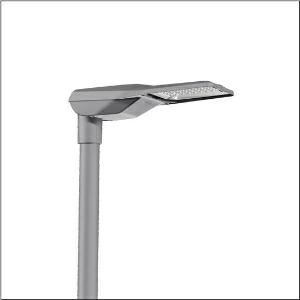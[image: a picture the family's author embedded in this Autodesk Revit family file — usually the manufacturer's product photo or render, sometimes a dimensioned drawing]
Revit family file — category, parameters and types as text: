
# Revit family: streetlight_sl_21_iq_mini___p1_0a_5xe2a31d08gb_969e
name_source: partatom
category: Lighting Fixtures
units: mm (PartAtom-declared; Revit-internal decimal feet)

## family parameters
Cut with Voids When Loaded = No
Host = Face
Light Source = No
Part Type = Normal
Room Calculation Point = No
Round Connector Dimension = Use Diameter
Shared = No

## types (1)
- --- (1 x LED, 5680 lm, 37.1 W, 3000K)
    Apparent Load = 37 VA
    CIE Flux Codes = 21 50 90 100 100
    Color Rendering = 70
    Color Temperature = 3000K
    Default Elevation = 1800 mm
    Description = Streetlight SL 21 iQ mini, mast luminaire, primary light control with lens, of PMMA, primary optical cover: cover, of toughened safety glass, transparent, light distribution: P1.0a, light emission: direct distribution, primary light characteristic: asymmetric, installation type: post-top, side-entry, LED, High Power LED, rated luminous flux: 5.680lm, luminous efficacy: 153lm/W, light colour: 730, colour temperature: 3000K, control: Auto-Match, Temp-Guard, Lumen-Switch, Night-Set, Smart-Wire, Light-Fading, Desk-Remote (wireless, voltage-free reading and setting of iQ features in the workshop via application-optimized NFC function/RFID function), optimised constant luminous flux control (CLO 2.0), presetting dimming linear, mains connection: 220..240V, AC, 50/60Hz, start of lifetime: 37W, end of service life: 39W, reduction: 18W, luminaire housing, of diecast aluminium, powder-coated, Siteco® metallic grey (DB 702S), corrosivity category C5 mid according to DIN EN ISO 12944, please order mast flange separately, inclination adjustable: 0°, 5°, 10°, 15°, sealing non-destructively replaceable, multi-level sealing system, length: 628mm, width: 235mm, height: 110mm, mast flange for spigot size: 42mm (side-entry): 5XC10008XM4, 60/48mm (side-entry/post-top): 5XC10108XM2, 76/60mm (side-entry/post-top): 5XC10108XM1, protection rating (complete): IP66, insulation class (complete): insulation class II (safety insulation), certification: CE, ENEC, ENEC+, VDE, impact resistance: IK09, permissible operating ambient temperature for outdoor applications: -40..+50°C, standard-compliant lighting for roads and squares, packaging unit: 1 piece

Light Distribution: P1.0a
    Height = 110 mm
    Lamp = 1 x LED
    Lamp Light Flux = 5680 lm
    Lamp Power = 37.1 W
    Lamp count = 1
    Length = 625 mm
    Luminous efficacy = 153 lm/W
    Manufacturer = Siteco
    ModVariant = No
    Model = 5XE2A31D08GB
    Number of Poles = 1
    OnlyDefault = Yes
    Power Factor = 1
    Product Name = Streetlight SL 21 iQ mini | P1.0a
    Product group = mast luminaire | pylon top
    ProductGroupID = 6100
    Protection Class = Protection class II
    Protection Degree = IP 66
    RLX_Detail_Level = 1
    RLX_Emergency_Light_Flux = 0 lm
    RLX_Emergency_Type = 0
    RLX_Emergency_Type_DB = No
    RlxData = <blob elided: 103505 chars, md5=d548e801>
    Socket = socket
    Standby Power = 0 W
    System Light Flux = 5680 lm
    System Power = 37 W
    Type Comments = factory setting: luminous flux: 100 % | dim-lin: 254 | 385 mA
    Type Image = l_1003519.jpg
    URL = http://relux.com
    VarID = @adj_120351
    Voltage = 0 V
    Weight = 0.00 kg
    Width = 234 mm

## geometry (parser evidence)
native form markers: Blend x4, Sweep x12
no freeform markers — native parametric forms only
